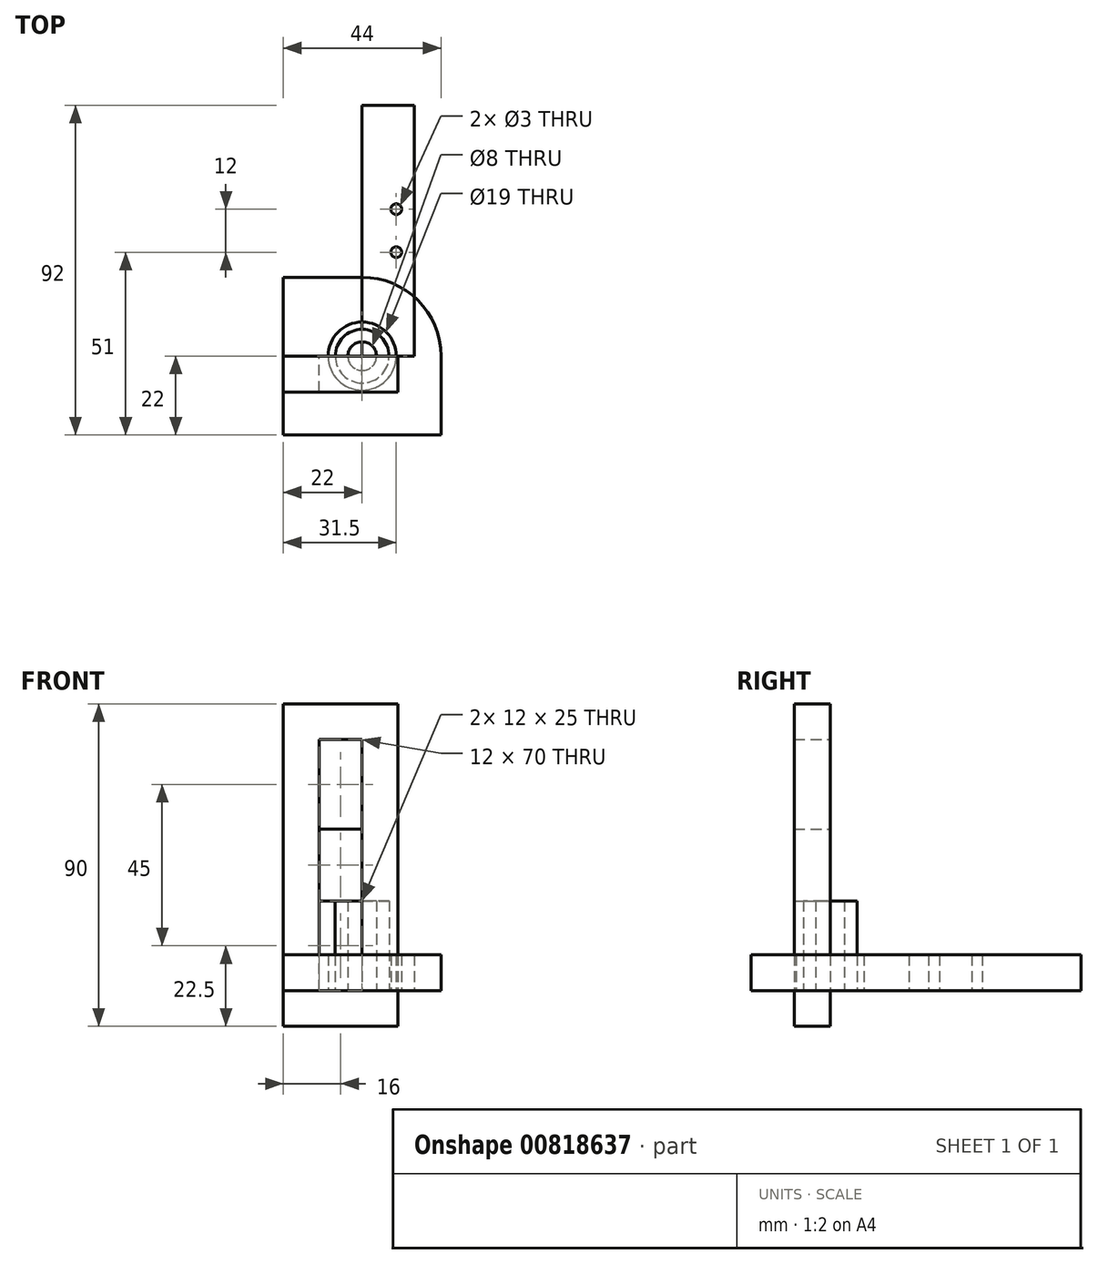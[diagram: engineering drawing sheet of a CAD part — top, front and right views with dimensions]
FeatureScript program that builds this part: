
annotation { "Feature Type Name" : "Feature", "Feature Type Description" : "" }
export const myFeature = defineFeature(function(context is Context, id is Id, definition is map)
    precondition{}
    {
        {
            var Q0;
            Q0=qCreatedBy(makeId("Top.planeOp"),FACE);
            var sketch = newSketch(context, id + "F0", { "sketchPlane" : qUnion([Q0])});
            skCircle(sketch, "E0", {"center": v(0, 0) * mm, "radius": 9.5 * mm});
            skLineSegment(sketch, "E1.bottom", {"start": v(0, 0) * mm, "end": v(-22, 0) * mm});
            skLineSegment(sketch, "E1.top", {"start": v(0, -22) * mm, "end": v(-22, -22) * mm});
            skLineSegment(sketch, "E1.left", {"start": v(0, 0) * mm, "end": v(0, -22) * mm});
            skLineSegment(sketch, "E1.right", {"start": v(-22, 0) * mm, "end": v(-22, -22) * mm});
            skLineSegment(sketch, "E2", {"start": v(-22, 0) * mm, "end": v(-22, 22) * mm});
            skLineSegment(sketch, "E3", {"start": v(0, -22) * mm, "end": v(22, -22) * mm});
            skLineSegment(sketch, "E4", {"start": v(-22, 22) * mm, "end": v(0, 22) * mm});
            skLineSegment(sketch, "E5", {"start": v(22, -22) * mm, "end": v(22, 0) * mm});
            skArc(sketch, "E6", {"start": v(0, 22) * mm, "mid": v(15.56, 15.56) * mm, "end": v(22, 0) * mm});
            skSolve(sketch);
        }
        {
            var Q0;
            {var subQ1=sQuery(id+"F0.wireOp",EDGE,"E1.top");Q0=makeQuery(id+"F0.imprint","IMPRINT",FACE,{"disambiguationData":[TD([[makeQuery(id+"F0.imprint","IMPRINT",EDGE,{"derivedFrom":subQ1}),-1.0]])]});}
            var Q1;
            {var subQ0=sQuery(id+"F0.wireOp",EDGE,"E2");Q1=makeQuery(id+"F0.imprint","IMPRINT",FACE,{"disambiguationData":[TD([[makeQuery(id+"F0.imprint","IMPRINT",EDGE,{"derivedFrom":subQ0}),-1.0]])]});}
            extrude(context, id + "F1", {"entities" : qUnion([Q0, Q1]), "depth" : 10 * mm, "offsetDistance" : 25 * mm});
        }
        {
            var Q0;
            Q0=qCreatedBy(makeId("Top.planeOp"),FACE);
            var sketch = newSketch(context, id + "F2", { "sketchPlane" : qUnion([Q0])});
            skLineSegment(sketch, "E7.bottom", {"start": v(0, 0) * mm, "end": v(326, 0) * mm});
            skLineSegment(sketch, "E7.top", {"start": v(0, 70) * mm, "end": v(326, 70) * mm});
            skLineSegment(sketch, "E7.left", {"start": v(0, 0) * mm, "end": v(0, 70) * mm});
            skLineSegment(sketch, "E7.right", {"start": v(326, 0) * mm, "end": v(326, 70) * mm});
            skLineSegment(sketch, "E8.bottom", {"start": v(0, 70) * mm, "end": v(7.5, 70) * mm});
            skLineSegment(sketch, "E8.left", {"start": v(0, 70) * mm, "end": v(0, 45) * mm});
            skLineSegment(sketch, "E9.bottom", {"start": v(0, 0) * mm, "end": v(7.5, 0) * mm});
            skLineSegment(sketch, "E9.left", {"start": v(0, 0) * mm, "end": v(0, 25) * mm});
            skLineSegment(sketch, "E10.bottom", {"start": v(326, 70) * mm, "end": v(318.5, 70) * mm});
            skLineSegment(sketch, "E10.top", {"start": v(326, 45) * mm, "end": v(318.5, 45) * mm});
            skLineSegment(sketch, "E10.left", {"start": v(326, 70) * mm, "end": v(326, 45) * mm});
            skLineSegment(sketch, "E10.right", {"start": v(318.5, 70) * mm, "end": v(318.5, 45) * mm});
            skLineSegment(sketch, "E11.bottom", {"start": v(326, 0) * mm, "end": v(318.5, 0) * mm});
            skLineSegment(sketch, "E11.top", {"start": v(326, 25) * mm, "end": v(318.5, 25) * mm});
            skLineSegment(sketch, "E11.left", {"start": v(326, 0) * mm, "end": v(326, 25) * mm});
            skLineSegment(sketch, "E11.right", {"start": v(318.5, 0) * mm, "end": v(318.5, 25) * mm});
            skLineSegment(sketch, "E12", {"start": v(0, 0) * mm, "end": v(4.5, 0) * mm});
            skLineSegment(sketch, "E13", {"start": v(4.5, 0) * mm, "end": v(14.5, 0) * mm});
            skLineSegment(sketch, "E14", {"start": v(14.5, 0) * mm, "end": v(14.5, 70) * mm});
            skLineSegment(sketch, "E15", {"start": v(0, 25) * mm, "end": v(14.5, 25) * mm, "construction": true});
            skLineSegment(sketch, "E16", {"start": v(14.5, 25) * mm, "end": v(14.5, 45) * mm, "construction": true});
            skLineSegment(sketch, "E17.bottom", {"start": v(14.5, 45) * mm, "end": v(4.5, 45) * mm});
            skLineSegment(sketch, "E17.top", {"start": v(14.5, 25) * mm, "end": v(4.5, 25) * mm});
            skLineSegment(sketch, "E17.left", {"start": v(14.5, 45) * mm, "end": v(14.5, 25) * mm});
            skLineSegment(sketch, "E17.right", {"start": v(4.5, 45) * mm, "end": v(4.5, 25) * mm});
            skLineSegment(sketch, "E18", {"start": v(14.5, 25) * mm, "end": v(14.5, 29) * mm});
            skLineSegment(sketch, "E19", {"start": v(14.5, 29) * mm, "end": v(14.5, 41) * mm});
            skLineSegment(sketch, "E20", {"start": v(14.5, 29) * mm, "end": v(9.5, 29) * mm});
            skLineSegment(sketch, "E21", {"start": v(14.5, 41) * mm, "end": v(9.5, 41) * mm});
            skCircle(sketch, "E22", {"center": v(9.5, 41) * mm, "radius": 1.5 * mm});
            skCircle(sketch, "E23", {"center": v(9.5, 29) * mm, "radius": 1.5 * mm});
            skSolve(sketch);
        }
        {
            var Q0;
            Q0=makeQuery(id+"F2.imprint","IMPRINT",FACE,{"disambiguationData":[TD([[makeQuery(id+"F2.imprint","IMPRINT",EDGE,{"derivedFrom":sQuery(id+"F2.wireOp",EDGE,"E7.bottom")}),1.0]])]});
            var Q1;
            Q1=makeQuery(id+"F2.imprint","IMPRINT",FACE,{"disambiguationData":[TD([[makeQuery(id+"F2.imprint","IMPRINT",EDGE,{"derivedFrom":sQuery(id+"F2.wireOp",EDGE,"E17.bottom")}),1.0]])]});
            extrude(context, id + "F3", {"entities" : qUnion([Q0, Q1]), "depth" : 10 * mm, "offsetDistance" : 25 * mm});
        }
        {
            var Q0;
            Q0=qCreatedBy(makeId("Top.planeOp"),FACE);
            var sketch = newSketch(context, id + "F4", { "sketchPlane" : qUnion([Q0])});
            skCircle(sketch, "E24", {"center": v(0, 0) * mm, "radius": 4 * mm});
            skCircle(sketch, "E25", {"center": v(0, 0) * mm, "radius": 7.5 * mm});
            skSolve(sketch);
        }
        {
            var Q0;
            Q0=makeQuery(id+"F4.imprint","IMPRINT",FACE,{"disambiguationData":[TD([[makeQuery(id+"F4.imprint","IMPRINT",EDGE,{"derivedFrom":sQuery(id+"F4.wireOp",EDGE,"E24")}),-1.0]])]});
            extrude(context, id + "F5", {"entities" : qUnion([Q0]), "depth" : 25 * mm, "offsetDistance" : 25 * mm});
        }
        {
            var Q0;
            Q0=qCreatedBy(makeId("Front.planeOp"),FACE);
            var sketch = newSketch(context, id + "F6", { "sketchPlane" : qUnion([Q0])});
            skLineSegment(sketch, "E26.bottom", {"start": v(0, 0) * mm, "end": v(-12, 0) * mm});
            skLineSegment(sketch, "E26.top", {"start": v(0, 25) * mm, "end": v(-12, 25) * mm});
            skLineSegment(sketch, "E26.left", {"start": v(0, 0) * mm, "end": v(0, 25) * mm});
            skLineSegment(sketch, "E26.right", {"start": v(-12, 0) * mm, "end": v(-12, 25) * mm});
            skLineSegment(sketch, "E27", {"start": v(0, 0) * mm, "end": v(0, 70) * mm});
            skLineSegment(sketch, "E28.bottom", {"start": v(0, 70) * mm, "end": v(-12, 70) * mm});
            skLineSegment(sketch, "E28.top", {"start": v(0, 45) * mm, "end": v(-12, 45) * mm});
            skLineSegment(sketch, "E28.left", {"start": v(0, 70) * mm, "end": v(0, 45) * mm});
            skLineSegment(sketch, "E28.right", {"start": v(-12, 70) * mm, "end": v(-12, 45) * mm});
            skLineSegment(sketch, "E29", {"start": v(0, 0) * mm, "end": v(10, 0) * mm});
            skLineSegment(sketch, "E30", {"start": v(10, 0) * mm, "end": v(10, -10) * mm});
            skLineSegment(sketch, "E31.bottom", {"start": v(10, -10) * mm, "end": v(-22, -10) * mm});
            skLineSegment(sketch, "E31.top", {"start": v(10, 80) * mm, "end": v(-22, 80) * mm});
            skLineSegment(sketch, "E31.left", {"start": v(10, -10) * mm, "end": v(10, 80) * mm});
            skLineSegment(sketch, "E31.right", {"start": v(-22, -10) * mm, "end": v(-22, 80) * mm});
            skLineSegment(sketch, "E32", {"start": v(-6, 25) * mm, "end": v(-6, 35) * mm});
            skLineSegment(sketch, "E33", {"start": v(-12, 45) * mm, "end": v(-12, 25) * mm});
            skSolve(sketch);
        }
        {
            var Q0;
            Q0=makeQuery(id+"F6.imprint","IMPRINT",FACE,{"disambiguationData":[TD([[makeQuery(id+"F6.imprint","IMPRINT",EDGE,{"derivedFrom":sQuery(id+"F6.wireOp",EDGE,"E26.bottom")}),1.0]])]});
            var Q1;
            {var subQ0=sQuery(id+"F6.wireOp",EDGE,"E28.top");Q1=makeQuery(id+"F6.imprint","IMPRINT",FACE,{"disambiguationData":[TD([[makeQuery(id+"F6.imprint","IMPRINT",EDGE,{"derivedFrom":subQ0}),1.0]])]});}
            extrude(context, id + "F7", {"entities" : qUnion([Q0, Q1]), "depth" : 10 * mm, "offsetDistance" : 25 * mm});
        }
        {
            var Q0;
            Q0=makeQuery(id+"F6.imprint","IMPRINT",FACE,{"disambiguationData":[TD([[makeQuery(id+"F6.imprint","IMPRINT",EDGE,{"derivedFrom":sQuery(id+"F6.wireOp",EDGE,"E26.bottom")}),1.0]])]});
            extrude(context, id + "F8", {"entities" : qUnion([Q0]), "depth" : 10 * mm, "offsetDistance" : 25 * mm});
        }
    });
